# Revit family: SWW8x180
name_source: partatom
category: Detail Items
revit_build: Autodesk Revit 2014 (Build: 20130308_1515(x64)
units: mm (PartAtom-declared; Revit-internal decimal feet)

## types (2) — shared parameters
Density = 0.04 kg
Description = Screws
EPD = https://www.strongtie.eu
ETA / DoP = https://www.strongtie.eu
Manufacturer = Simpson Strong-Tie
Model = SWW8x180
Model Disclaimer = Contact Simpson Strong-Tie Company  for more information
Model ID = 0326619404762450741270297207587616444566
Name = SWW8x180
ObjectType = SWW8x180
Product Material = ElectroGalvanised
Product Type = Screws
Reference = 72113
Technical datasheet = https://www.strongtie.eu
URL = www.strongtie.eu
UniClass Number = Pr_20_29_76_98
UniClass Title = Wood screws

## per-type parameters (varying)
| type | _visiblefront | _visibletop |
| SST_SWW8x180_Top | No | Yes |
| SST_SWW8x180_Front | Yes | No |

## geometry (parser evidence)
native form markers: Sweep x2
no freeform markers — native parametric forms only
